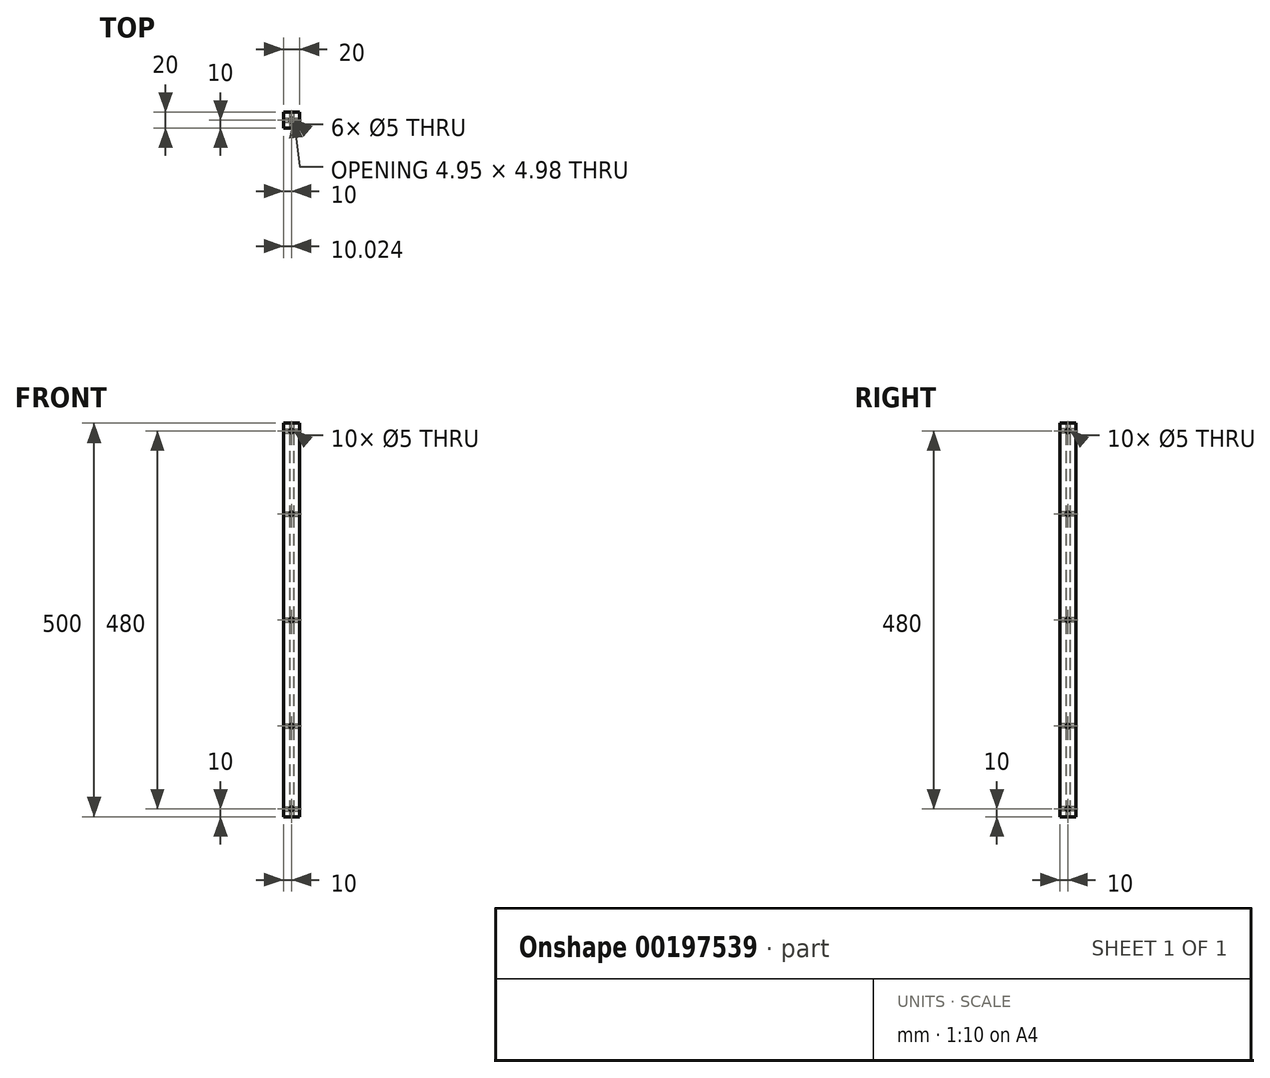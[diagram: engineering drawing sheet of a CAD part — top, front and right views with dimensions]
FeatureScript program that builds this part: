
annotation { "Feature Type Name" : "Feature", "Feature Type Description" : "" }
export const myFeature = defineFeature(function(context is Context, id is Id, definition is map)
    precondition{}
    {
        {
            var Q0;
            Q0=qCreatedBy(makeId("Top.planeOp"),FACE);
            var sketch = newSketch(context, id + "F0", { "sketchPlane" : qUnion([Q0])});
            skLineSegment(sketch, "E0.bottom", {"start": v(-10, 10) * mm, "end": v(10, 10) * mm});
            skLineSegment(sketch, "E0.top", {"start": v(-10, -10) * mm, "end": v(10, -10) * mm});
            skLineSegment(sketch, "E0.left", {"start": v(-10, 10) * mm, "end": v(-10, -10) * mm});
            skLineSegment(sketch, "E0.right", {"start": v(10, 10) * mm, "end": v(10, -10) * mm});
            skCircle(sketch, "E1", {"center": v(0, 0) * mm, "radius": 2.5 * mm});
            skSolve(sketch);
        }
        {
            var Q0;
            Q0=qSketchRegion(id+"F0",true);
            extrude(context, id + "F1", {"entities" : qUnion([Q0]), "depth" : 500 * mm});
        }
        {
            var Q0;
            Q0=makeQuery(id+"F1.opExtrude","SWEPT_FACE",FACE,{"disambiguationData":[OSD([sQuery(id+"F0.wireOp",EDGE,"E0.right")])]});
            var sketch = newSketch(context, id + "F2", { "sketchPlane" : qUnion([Q0])});
            skCircle(sketch, "E2", {"center": v(0, 10) * mm, "radius": 2.5 * mm});
            skCircle(sketch, "E3", {"center": v(0, 490) * mm, "radius": 2.5 * mm});
            skCircle(sketch, "E4", {"center": v(0, 250) * mm, "radius": 2.5 * mm});
            skPoint(sketch, "E4.centerSnap0", {"position": v(-10, 250) * mm});
            skCircle(sketch, "E5", {"center": v(0, 115.13) * mm, "radius": 2.5 * mm});
            skCircle(sketch, "E6", {"center": v(0, 384.87) * mm, "radius": 2.5 * mm});
            skSolve(sketch);
        }
        {
            var Q0;
            Q0=qSketchRegion(id+"F2",true);
            extrude(context, id + "F3", {"entities" : qUnion([Q0]), "operationType" : NewBodyOperationType.REMOVE, "endBound" : BoundingType.THROUGH_ALL, "oppositeDirection" : true, "depth" : 25 * mm});
        }
        {
            var Q0;
            Q0=makeQuery(id+"F1.opExtrude","SWEPT_FACE",FACE,{"disambiguationData":[OSD([sQuery(id+"F0.wireOp",EDGE,"E0.top")])]});
            var sketch = newSketch(context, id + "F4", { "sketchPlane" : qUnion([Q0])});
            skCircle(sketch, "E7", {"center": v(0, 250) * mm, "radius": 2.5 * mm});
            skPoint(sketch, "E7.centerSnap0", {"position": v(-10, 250) * mm});
            skCircle(sketch, "E8", {"center": v(0, 490) * mm, "radius": 2.5 * mm});
            skCircle(sketch, "E9", {"center": v(0, 10) * mm, "radius": 2.5 * mm});
            skCircle(sketch, "E10", {"center": v(0, 115.13) * mm, "radius": 2.5 * mm});
            skCircle(sketch, "E11", {"center": v(0, 384.87) * mm, "radius": 2.5 * mm});
            skSolve(sketch);
        }
        {
            var Q0;
            Q0=qSketchRegion(id+"F4",true);
            extrude(context, id + "F5", {"entities" : qUnion([Q0]), "operationType" : NewBodyOperationType.REMOVE, "endBound" : BoundingType.THROUGH_ALL, "oppositeDirection" : true, "depth" : 25 * mm});
        }
    });
